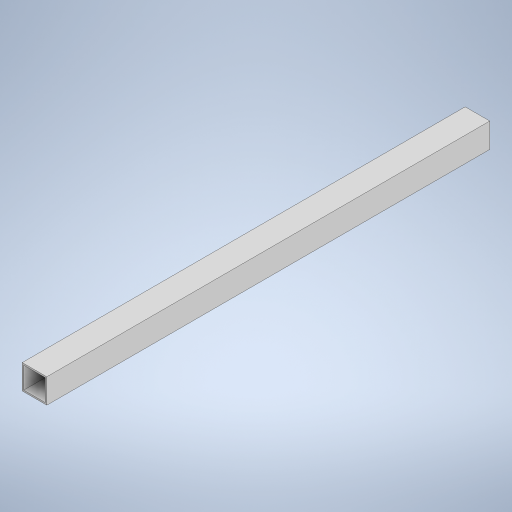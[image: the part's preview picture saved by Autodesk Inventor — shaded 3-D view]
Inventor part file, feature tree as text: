
AUTODESK INVENTOR PART (.ipt)
format: ipt  version: 2024 (Build 280153000, 153)  size: 229,888 bytes
history: native  units: in
note: dims shown in document units (in); Inventor stores cm internally (conversion verified against a paired STEP export)
features: extrude x1, sketch x1
ambient origin geometry x8: Origin, YZ Plane, XZ Plane, XY Plane, X Axis, Y Axis, Z Axis, Center Point
bodies: Solid1 (feature_tree)
feature tree (2):
  extrude  "Extrusion1"  Depth=1.0in
  sketch  "Sketch1"  dims[d0=1.0in d1=1.0in d2=0.0625in d3=18.0in d4=0.0in]
